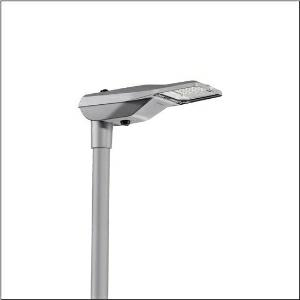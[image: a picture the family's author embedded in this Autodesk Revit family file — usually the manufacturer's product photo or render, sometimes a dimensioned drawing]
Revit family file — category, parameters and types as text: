
# Revit family: streetlight_sl_21_micro___st1_5a_5xe1p33t08db_27e3
name_source: partatom
category: Lighting Fixtures
units: mm (PartAtom-declared; Revit-internal decimal feet)

## family parameters
Cut with Voids When Loaded = No
Host = Face
Light Source = No
Part Type = Normal
Room Calculation Point = No
Round Connector Dimension = Use Diameter
Shared = No

## types (1)
- --- (1 x LED, 5020 lm, 39.1 W, 3000K)
    Apparent Load = 39 VA
    CIE Flux Codes = 22 53 95 100 100
    Color Rendering = 70
    Color Temperature = 3000K
    Default Elevation = 1800 mm
    Description = Streetlight SL 21 micro, mast luminaire, primary light control with lens, of PMMA, primary optical cover: cover, of toughened safety glass, transparent, light distribution: ST1.5a, light emission: direct distribution, primary light characteristic: asymmetric, installation type: side-entry, post-top, LED, High Power LED, rated luminous flux: 5.020lm, luminous efficacy: 128lm/W, light colour: 730, colour temperature: 3000K, control gear: D4i, control: flexible luminous flux parameterisation, time-dependent luminous flux control, constant luminous flux control, overheat protection, pre-setting: logarithmic dimming characteristic, mains connection: 220..240V, AC, 50/60Hz, start of lifetime: 39W, end of service life: 41W, reduction: 18W, luminaire housing, of diecast aluminium, powder-coated, Siteco® metallic grey (DB 702S), corrosivity category C5 mid according to DIN EN ISO 12944, please order mast flange separately, inclination adjustable: 0°, 5°, 10°, 15°, sealing non-destructively replaceable, multi-level sealing system, length: 528mm, width: 235mm, height: 110mm, mast flange for spigot size: 42mm (side-entry): 5XC10008XM4, 60/48mm (side-entry/post-top): 5XC10108XM2, 76/60mm (side-entry/post-top): 5XC10108XM1, Smart Interface below and above, protection rating (complete): IP66, insulation class (complete): insulation class II (safety insulation), certification: CE, ENEC, ENEC+, VDE, impact resistance: IK10, permissible operating ambient temperature for outdoor applications: -40..+50°C, standard-compliant lighting for roads and squares, packaging unit: 1 piece

Light Distribution: ST1.5a
    Height = 110 mm
    Lamp = 1 x LED
    Lamp Light Flux = 5020 lm
    Lamp Power = 39.1 W
    Lamp count = 1
    Length = 528 mm
    Luminous efficacy = 128 lm/W
    Manufacturer = Siteco
    ModVariant = No
    Model = 5XE1P33T08DB
    Number of Poles = 1
    OnlyDefault = Yes
    Power Factor = 1
    Product Name = Streetlight SL 21 micro | ST1.5a
    Product group = mast luminaire | pylon top
    ProductGroupID = 6100
    Protection Class = Protection class II
    Protection Degree = IP 66
    RLX_Detail_Level = 1
    RLX_Emergency_Light_Flux = 0 lm
    RLX_Emergency_Type = 0
    RLX_Emergency_Type_DB = No
    RlxData = <blob elided: 101933 chars, md5=a54f7fd5>
    Socket = socket
    Standby Power = 0 W
    System Light Flux = 5020 lm
    System Power = 39 W
    Type Comments = factory setting: luminous flux: 100 % | dim-lin: 254 | 765 mA
    Type Image = l_1007239.jpg
    URL = http://relux.com
    VarID = @adj_153712
    Voltage = 0 V
    Weight = 0.00 kg
    Width = 235 mm

## geometry (parser evidence)
native form markers: Blend x4, Sweep x9
no freeform markers — native parametric forms only
